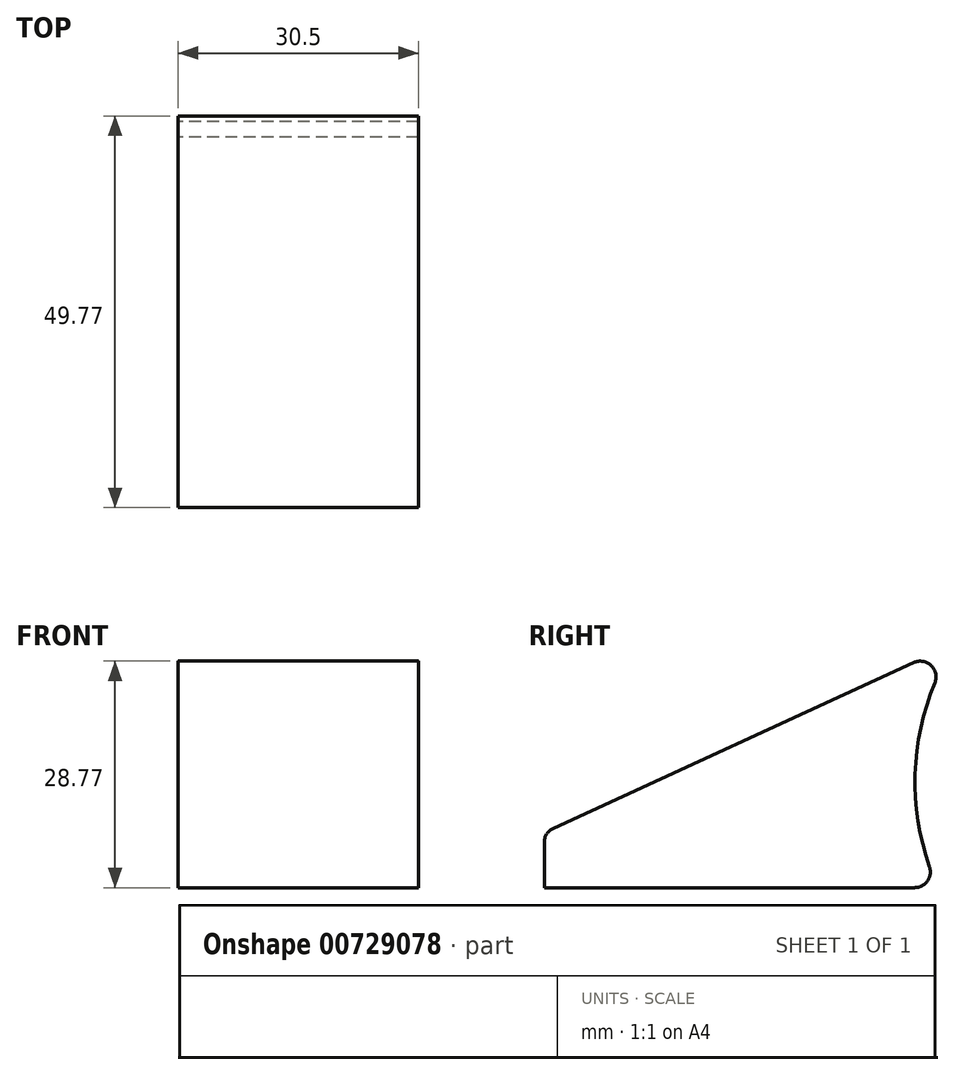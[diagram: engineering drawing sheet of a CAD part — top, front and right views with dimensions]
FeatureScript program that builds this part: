
annotation { "Feature Type Name" : "Feature", "Feature Type Description" : "" }
export const myFeature = defineFeature(function(context is Context, id is Id, definition is map)
    precondition{}
    {
        {
            var Q0;
            Q0=qCreatedBy(makeId("Right.planeOp"),FACE);
            var sketch = newSketch(context, id + "F0", { "sketchPlane" : qUnion([Q0])});
            skLineSegment(sketch, "E0", {"start": v(0, 0) * mm, "end": v(50, 0) * mm});
            skLineSegment(sketch, "E1", {"start": v(52.26, 31.04) * mm, "end": v(0, 7) * mm});
            skLineSegment(sketch, "E2", {"start": v(0, 7) * mm, "end": v(0, 0) * mm});
            skPoint(sketch, "E3.visualSharp", {"position": v(0, 7) * mm});
            skLineSegment(sketch, "E4", {"start": v(1.75, 7.8) * mm, "end": v(-2.66, 5.78) * mm, "construction": true});
            skLineSegment(sketch, "E5", {"start": v(-2.66, 5.78) * mm, "end": v(0, 0) * mm, "construction": true});
            skLineSegment(sketch, "E6", {"start": v(0, 0) * mm, "end": v(0, 0) * mm});
            skArc(sketch, "E7", {"start": v(52.26, 31.04) * mm, "mid": v(47.19, 15.8) * mm, "end": v(50, 0) * mm});
            skSolve(sketch);
        }
        {
            var Q0;
            Q0 = qSketchRegion(id + "F0", true);
            extrude(context, id + "F1", {"entities" : qUnion([Q0]), "depth" : 30.5 * mm, "offsetDistance" : 25 * mm});
        }
        {
            var Q0;
            Q0=makeQuery(id+"F1.opExtrude","SWEPT_EDGE",EDGE,{"disambiguationData":[OSD([sQuery(id+"F0.wireOp",EDGE,"E1"),sQuery(id+"F0.wireOp",EDGE,"E7")])]});
            fillet(context, id + "F2", {"entities" : qUnion([Q0]), "radius" : 2 * mm, "tangentPropagation" : true, "allowEdgeOverflow" : false});
        }
        {
            var Q0;
            Q0=makeQuery(id+"F1.opExtrude","SWEPT_EDGE",EDGE,{"disambiguationData":[OSD([sQuery(id+"F0.wireOp",EDGE,"E1"),sQuery(id+"F0.wireOp",EDGE,"6b212970-120f-4ac5-9390-09a52b7c415f.trimOffspring")])]});
            var Q1;
            Q1=makeQuery(id+"F1.opExtrude","SWEPT_EDGE",EDGE,{"disambiguationData":[OSD([sQuery(id+"F0.wireOp",EDGE,"E7"),sQuery(id+"F0.wireOp",EDGE,"6b212970-120f-4ac5-9390-09a52b7c415f.trimOffspring")])]});
            fillet(context, id + "F3", {"entities" : qUnion([Q0, Q1]), "radius" : 2 * mm, "tangentPropagation" : true, "allowEdgeOverflow" : false});
        }
    });
